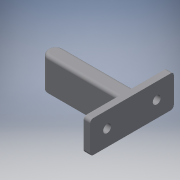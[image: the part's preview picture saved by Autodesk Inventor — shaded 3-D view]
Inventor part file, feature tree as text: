
AUTODESK INVENTOR PART (.ipt)
format: ipt  version: 2018 (Build 220112000, 112)  size: 206,848 bytes
history: native  units: mm
features: extrude x5, sketch x5, other x5, reference x4, fillet x2, plane x1
ambient origin geometry x8: Origin, YZ Plane, XZ Plane, XY Plane, X Axis, Y Axis, Z Axis, Center Point
bodies: Solid1 (feature_tree)
feature tree (22):
  extrude  "Extrusion1"  Depth=10.0mm TaperAngle=0.0deg
  sketch  "Sketch2"  dims[d4=2.5mm d5=2.5mm]
  plane  "Work Plane1"
  extrude  "Extrusion2"  Depth=2.5mm
  extrude  "Extrusion3"  Depth=10.0mm TaperAngle=0.0deg
  extrude  "Extrusion4"  Depth=1.0mm
  extrude  "Extrusion5"  [1 undecoded]
  fillet  "Fillet2"  [1 undecoded]
  fillet  "Fillet3"  [1 undecoded]
  sketch  "Sketch1"  dims[d0=10.0mm d1=0.0mm d2=10.0mm d3=0.0mm]
  reference  "Reference1"
  reference  "Reference2"
  reference  "Reference3"
  sketch  "Sketch3"  dims[d6=2.0mm d7=0.0mm d9=10.0mm d10=0.0mm]
  reference  "Reference4"
  sketch  "Sketch4"  dims[d11=10.0mm d12=0.0mm d13=1.0mm]
  sketch  "Sketch5"  dims[d14=1.0mm]
  other  "<userpath>\OneDrive\Documents\Inventor\TSA\2018\Animatronics\Tortoise\AssemblyTURTLE.iam"
  other  "AssemblyTURTLE.iam"
  other  "GuideArm:1"
  other  "Frame - Copy:1"
  other  "Supporter:1"
note: 3 required parameter values undecoded (feature->parameter linkage not recoverable at this tier; creation-order binding heuristic only, values carry confidence <= 0.55)
